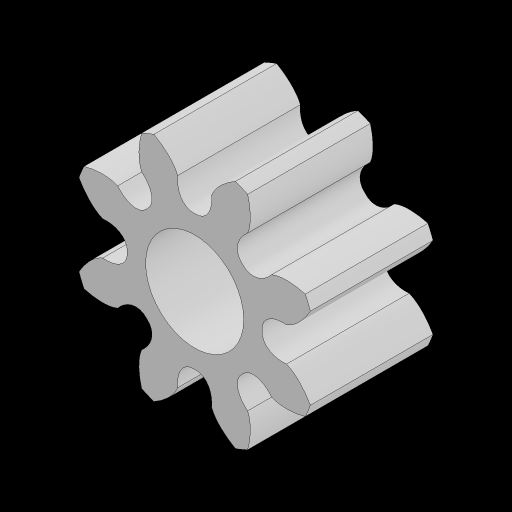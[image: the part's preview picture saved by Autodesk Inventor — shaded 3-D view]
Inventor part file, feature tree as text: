
AUTODESK INVENTOR PART (.ipt)
format: ipt  version: 2023.2 (Build 272271030, 271C)  size: 200,192 bytes
history: native  units: mm
features: extrude x3, sketch x2, pattern_circular x1
ambient origin geometry x8: Origin, YZ Plane, XZ Plane, XY Plane, X Axis, Y Axis, Z Axis, Center Point
bodies: Solid1 (feature_tree)
feature tree (6):
  sketch  "Sketch1"  dims[d0=5.0mm d1=0.0mm d2=4.0mm]
  extrude  "Extrusion1"  Depth=4.0mm
  sketch  "Sketch2"  dims[d3=0.0mm d4=0.0mm d5=80.0mm d6=360.0deg d8=0.0mm d9=0.0mm]
  extrude  "Extrusion2"  Depth=80.0mm TaperAngle=360.0deg
  pattern_circular  "Circular Pattern1"  [2 undecoded]
  extrude  "Extrusion3"  [1 undecoded]
note: 3 required parameter values undecoded (feature->parameter linkage not recoverable at this tier; creation-order binding heuristic only, values carry confidence <= 0.55)
